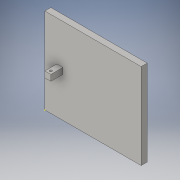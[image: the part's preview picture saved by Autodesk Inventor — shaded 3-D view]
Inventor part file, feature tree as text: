
AUTODESK INVENTOR PART (.ipt)
format: ipt  version: 2016 (Build 200138000, 138)  size: 100,864 bytes
history: native  units: in
note: dims shown in document units (in); Inventor stores cm internally (conversion verified against a paired STEP export)
features: sketch x4, extrude x2, hole x1
ambient origin geometry x8: Origin, YZ Plane, XZ Plane, XY Plane, X Axis, Y Axis, Z Axis, Center Point
bodies: Solid1 (feature_tree)
feature tree (7):
  extrude  "Extrusion1"  Depth=1.78in
  sketch  "Sketch3"  dims[d2=0.125in d3=0.0in d12=0.125in]
  sketch  "Sketch4"  dims[d13=0.125in d14=0.25in d15=0.0in]
  extrude  "Extrusion3"  Depth=0.125in
  hole  "Hole1"  [1 undecoded]
  sketch  "Sketch1"  dims[d0=2.0in d1=1.78in]
  sketch  "Sketch5"  dims[d16=0.063in d17=0.063in d18=0.05in d19=0.75in d20=0.375in d21=0.25in d22=0.5635in d23=1.0in d24=0.8108in]
note: 1 required parameter value undecoded (feature->parameter linkage not recoverable at this tier; creation-order binding heuristic only, values carry confidence <= 0.55)
